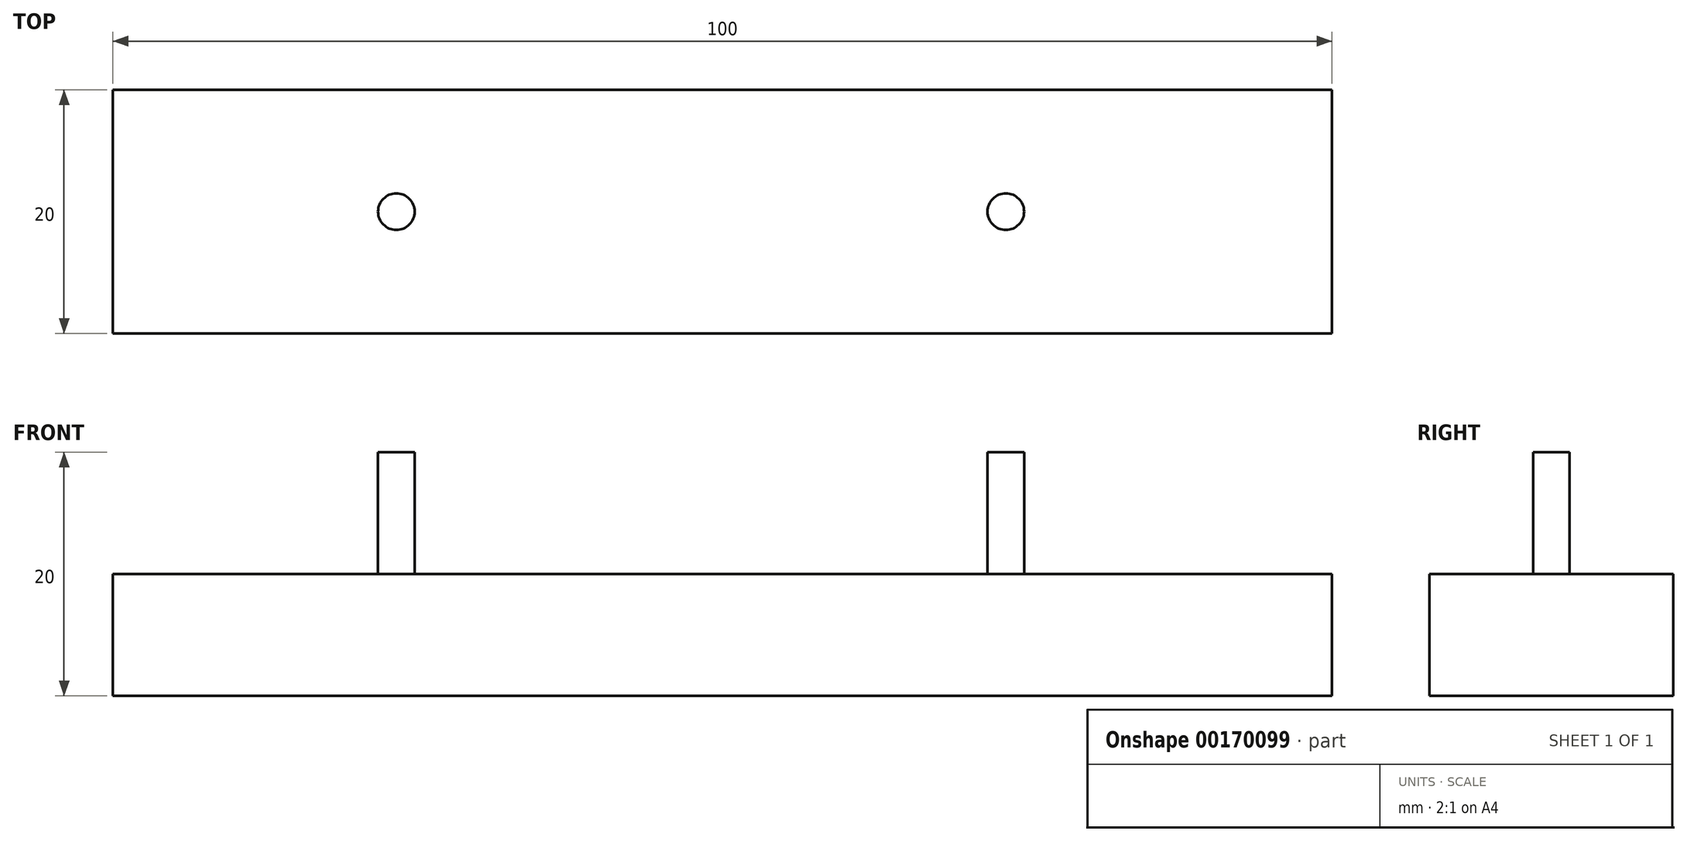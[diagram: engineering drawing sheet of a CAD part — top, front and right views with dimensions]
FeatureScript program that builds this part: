
annotation { "Feature Type Name" : "Feature", "Feature Type Description" : "" }
export const myFeature = defineFeature(function(context is Context, id is Id, definition is map)
    precondition{}
    {
        {
            var Q0;
            Q0=qCreatedBy(makeId("Top.planeOp"),FACE);
            var sketch = newSketch(context, id + "F0", { "sketchPlane" : qUnion([Q0])});
            skLineSegment(sketch, "E0.bottom", {"start": v(50, 10) * mm, "end": v(-50, 10) * mm});
            skLineSegment(sketch, "E0.top", {"start": v(50, -10) * mm, "end": v(-50, -10) * mm});
            skLineSegment(sketch, "E0.left", {"start": v(50, 10) * mm, "end": v(50, -10) * mm});
            skLineSegment(sketch, "E0.right", {"start": v(-50, 10) * mm, "end": v(-50, -10) * mm});
            skPoint(sketch, "E0.middle", {"position": v(0, 0) * mm});
            skSolve(sketch);
        }
        {
            var Q0;
            Q0=makeQuery(id+"F0.imprint","IMPRINT",FACE,{"disambiguationData":[TD([[makeQuery(id+"F0.imprint","IMPRINT",EDGE,{"derivedFrom":sQuery(id+"F0.wireOp",EDGE,"E0.bottom")}),1.0]])]});
            extrude(context, id + "F1", {"entities" : qUnion([Q0]), "depth" : 10 * mm});
        }
        {
            var Q0;
            Q0=makeQuery(id+"F1.opExtrude","CAP_FACE",FACE,{"disambiguationData":[OSD([sQuery(id+"F0.wireOp",EDGE,"E0.bottom"),sQuery(id+"F0.wireOp",EDGE,"E0.top"),sQuery(id+"F0.wireOp",EDGE,"E0.left"),sQuery(id+"F0.wireOp",EDGE,"E0.right")])],"isStart":false});
            var sketch = newSketch(context, id + "F2", { "sketchPlane" : qUnion([Q0])});
            skCircle(sketch, "E1", {"center": v(-26.75, 0) * mm, "radius": 1.5 * mm});
            skCircle(sketch, "E2", {"center": v(23.25, 0) * mm, "radius": 1.5 * mm});
            skSolve(sketch);
        }
        {
            var Q0;
            Q0=makeQuery(id+"F2.imprint","IMPRINT",FACE,{"disambiguationData":[TD([[makeQuery(id+"F2.imprint","IMPRINT",EDGE,{"derivedFrom":sQuery(id+"F2.wireOp",EDGE,"E1")}),1.0]])]});
            var Q1;
            Q1=makeQuery(id+"F2.imprint","IMPRINT",FACE,{"disambiguationData":[TD([[makeQuery(id+"F2.imprint","IMPRINT",EDGE,{"derivedFrom":sQuery(id+"F2.wireOp",EDGE,"E2")}),1.0]])]});
            extrude(context, id + "F3", {"entities" : qUnion([Q0, Q1]), "operationType" : NewBodyOperationType.ADD, "depth" : 10 * mm});
        }
    });
